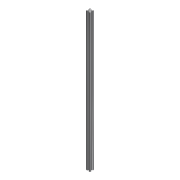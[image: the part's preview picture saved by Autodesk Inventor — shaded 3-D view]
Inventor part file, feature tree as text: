
AUTODESK INVENTOR PART (.ipt)
format: ipt  version: 2019 (Build 230136000, 136)  size: 183,808 bytes
history: native  units: mm
features: other x1, extrude x1, fillet x1, sketch x1
ambient origin geometry x8: Origin, YZ Plane, XZ Plane, XY Plane, X Axis, Y Axis, Z Axis, Center Point
bodies: Body1 (feature_tree)
feature tree (4):
  other  "솔리드1"
  extrude  "돌출1"  Depth=20.0mm
  fillet  "모깎기1"  Radius=20.0mm
  sketch  "스케치1"
